# Revit family: 0045155 Feilo Sylvania Lighting Fixture START BATTEN  IP65 26W 1500 4K
name_source: partatom
category: Lighting Fixtures
revit_build: Autodesk Revit 2017 (Build: 20190507_1515(x64)
units: mm (PartAtom-declared; Revit-internal decimal feet)

## family parameters
Cut with Voids When Loaded = No
Host = Face
Light Source = Yes
OmniClass Number = 23.80.70.00
OmniClass Title = Lighting
Part Type = Normal
Room Calculation Point = No
Round Connector Dimension = Use Diameter
Shared = No

## types (1)
- 0045155 START BATTEN  IP65 26W 1500 4K
    Apparent Load = 26 VA
    Assembly Code = D5020200
    AssetType = Fixed
    ClassificationName = Uniclass2015
    ClassificationValue = EF_70_80
    Color Filter = 16777215
    Cost = 0 $
    Default Elevation = 1219 mm
    Description = The new upgraded Start Batten IP65 ( upgraded version of Batten LED LINK) is a versatile range of slimline LED waterproof luminaires that provide an ideal solution for interior and exterior applications such as workshops, garages and outdoor covered spaces. The  design allows the luminaire to be easily linked to another luminaire through an IP65 rated connector. The performance of the range  has been significantly improved ,  for example Start Twin Batten IP65 LED delivers  a performance of up to 6000lm (125lm/W). Available in 1200mm and 1500mm lengths (approx.) - the product can be a slimline replacement for single and twin 36W/58W fluorescent waterproof battens.
    Dimming Lamp Color Temperature Shift = <None>
    DocumentationLiterature = http://www.sylvania-lighting.com
    DurationUnit = hours
    ElectricShockClassification = Class II
    Emit Shape Visible in Rendering = No
    Emit from Rectangle Length = 1338 mm
    Emit from Rectangle Width = 25 mm  [stored 0.082021 ft]
    ExpectedLife = 50000
    IfcExportAs = IfcLightFixtureType
    IfcExportType = IfcLightFixtureType
    ImpactProtectionIndex = IK08
    IngressProtection = IP65
    InputNominalFrequency = 50/60 Hz
    InputVoltage = 220-240V~
    Keynote = 16500
    L1_FEILO = 1588 mm
    L2_FEILO = 1543 mm
    L3_FEILO = 1378 mm
    Lamp = LED
    LampColourRenderingIndex = 80
    LampColourTemperature = 4000 K
    LampNominalLuminous = 3200 lm
    LampsType = LED
    LightOutputRatio = 100
    Long_FEILO = Yes
    LuminousEfficacy = 123 lm/W
    Manufacturer = Feilo Sylvania
    ManufacturerName = Feilo Sylvania
    Material = polycarbonate housing, pc diffuser
    Material_1_FEILO = Body-Sylvania-StartBatten
    Material_2_FEILO = Diffuser-Sylvania-StartBatten
    Material_3_FEILO = <By Category>
    Material_4_FEILO = <By Category>
    Model = START BATTEN  IP65 26W 1500 4K
    ModelNumber = 0045155
    ModelReference = START BATTEN  IP65 26W 1500 4K
    Name = START BATTEN  IP65 26W 1500 4K
    NominalDepth = 42 mm
    NominalHeight = 53 mm
    NominalLength = 1500 mm
    Photometric Web File = 0045155.ies
    PowerConsumption = 26 W
    PowerFactor = 0
    RadiusBody_FEILO = 22 mm
    RadiusGlandInner_FEILO = 5 mm  [stored 0.0164042 ft]
    RadiusGlandOuter_FEILO = 10 mm  [stored 0.0328084 ft]
    Tilt Angle = -90.00°
    Type Image = <None>
    TypeName = START BATTEN  IP65 26W 1500 4K
    URL = http://www.sylvania-lighting.com
    Voltage = 230 V
    Weight = 9.132 kg

note: [stored X ft] marks values corroborated as IEEE doubles in the binary element streams (Revit-internal decimal feet)

## geometry (parser evidence)
native form markers: Sweep x2
no freeform markers — native parametric forms only
